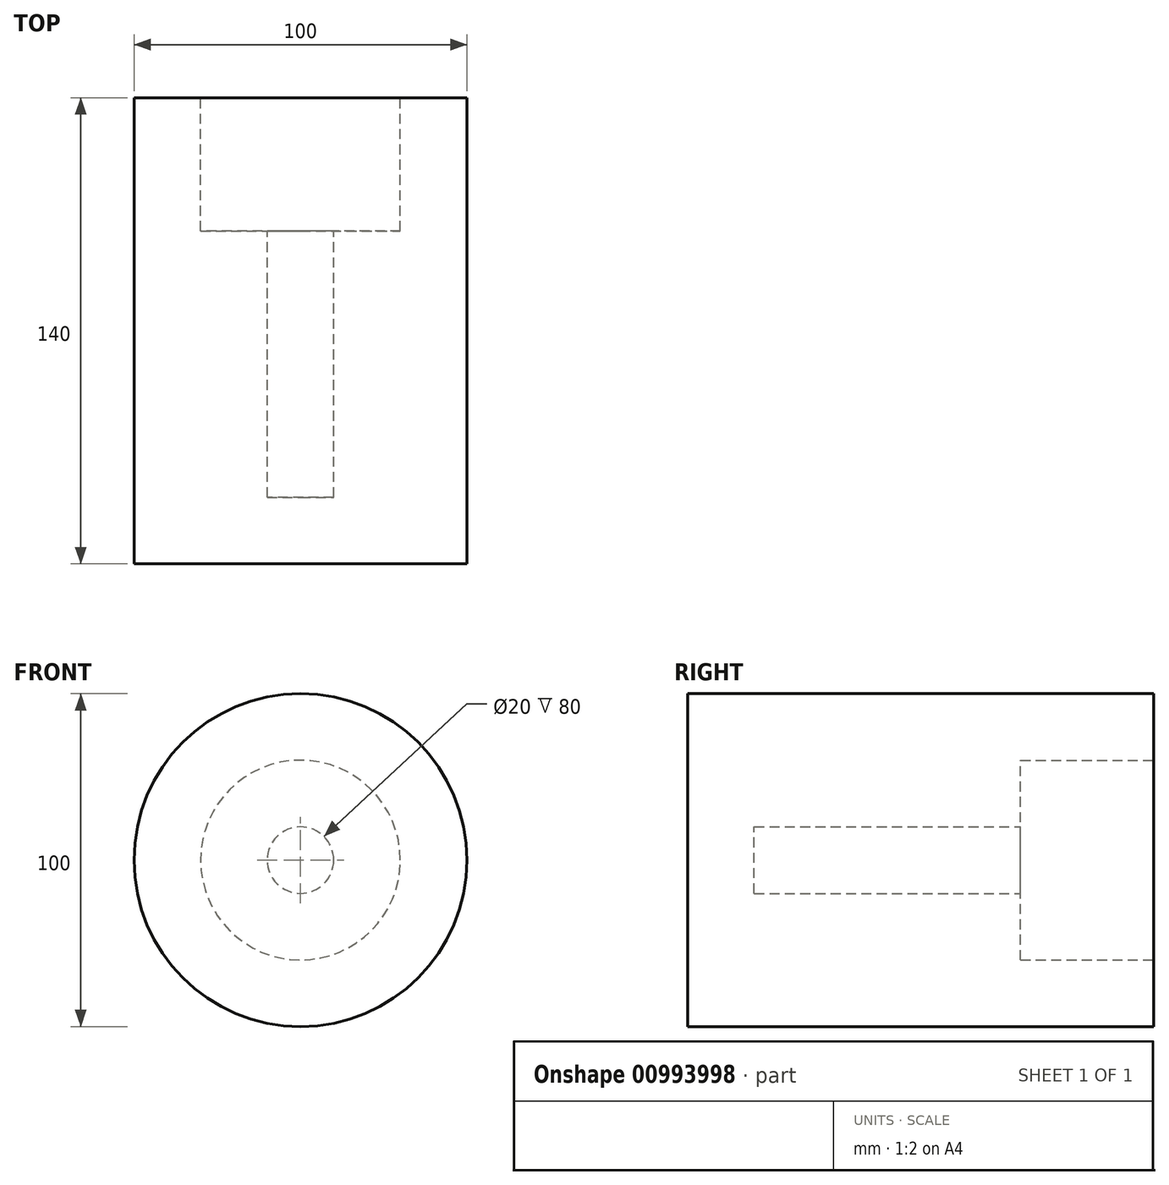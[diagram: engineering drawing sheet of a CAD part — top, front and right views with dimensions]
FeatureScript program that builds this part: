
annotation { "Feature Type Name" : "Feature", "Feature Type Description" : "" }
export const myFeature = defineFeature(function(context is Context, id is Id, definition is map)
    precondition{}
    {
        {
            var Q0;
            Q0=qCreatedBy(makeId("Front.planeOp"),FACE);
            var sketch = newSketch(context, id + "F0", { "sketchPlane" : qUnion([Q0])});
            skCircle(sketch, "E0", {"center": v(0, 0) * mm, "radius": 50 * mm});
            skCircle(sketch, "E1", {"center": v(0, 0) * mm, "radius": 30 * mm});
            skCircle(sketch, "E2", {"center": v(0, 0) * mm, "radius": 10 * mm});
            skSolve(sketch);
        }
        {
            var Q0;
            Q0=makeQuery(id+"F0.imprint","IMPRINT",FACE,{"disambiguationData":[TD([[makeQuery(id+"F0.imprint","IMPRINT",EDGE,{"derivedFrom":sQuery(id+"F0.wireOp",EDGE,"E0")}),1.0]])]});
            var Q1;
            Q1=makeQuery(id+"F0.imprint","IMPRINT",FACE,{"disambiguationData":[TD([[makeQuery(id+"F0.imprint","IMPRINT",EDGE,{"derivedFrom":sQuery(id+"F0.wireOp",EDGE,"E1")}),1.0]])]});
            var Q2;
            Q2=makeQuery(id+"F0.imprint","IMPRINT",FACE,{"disambiguationData":[TD([[makeQuery(id+"F0.imprint","IMPRINT",EDGE,{"derivedFrom":sQuery(id+"F0.wireOp",EDGE,"E2")}),1.0]])]});
            extrude(context, id + "F1", {"entities" : qUnion([Q0, Q1, Q2]), "depth" : 140 * mm, "offsetDistance" : 25 * mm});
        }
        {
            var Q0;
            Q0=makeQuery(id+"F0.imprint","IMPRINT",FACE,{"disambiguationData":[TD([[makeQuery(id+"F0.imprint","IMPRINT",EDGE,{"derivedFrom":sQuery(id+"F0.wireOp",EDGE,"E1")}),1.0]])]});
            var Q1;
            Q1=makeQuery(id+"F0.imprint","IMPRINT",FACE,{"disambiguationData":[TD([[makeQuery(id+"F0.imprint","IMPRINT",EDGE,{"derivedFrom":sQuery(id+"F0.wireOp",EDGE,"E2")}),1.0]])]});
            extrude(context, id + "F2", {"entities" : qUnion([Q0, Q1]), "operationType" : NewBodyOperationType.REMOVE, "depth" : 40 * mm, "offsetDistance" : 25 * mm});
        }
        {
            var Q0;
            Q0=makeQuery(id+"F0.imprint","IMPRINT",FACE,{"disambiguationData":[TD([[makeQuery(id+"F0.imprint","IMPRINT",EDGE,{"derivedFrom":sQuery(id+"F0.wireOp",EDGE,"E2")}),1.0]])]});
            extrude(context, id + "F3", {"entities" : qUnion([Q0]), "operationType" : NewBodyOperationType.REMOVE, "depth" : 120 * mm, "offsetDistance" : 25 * mm});
        }
    });
